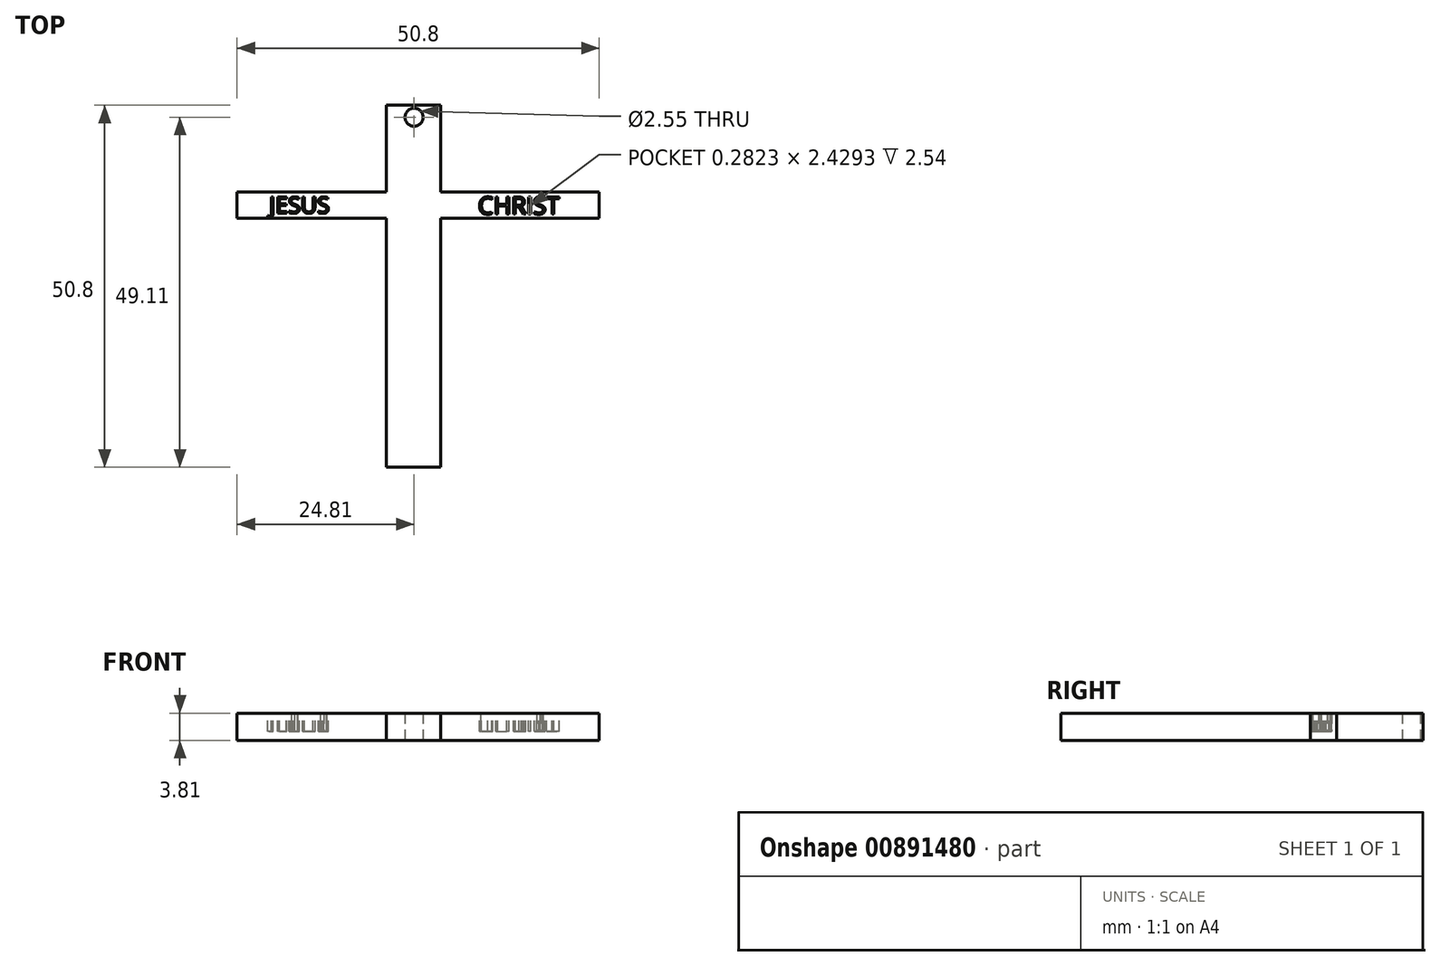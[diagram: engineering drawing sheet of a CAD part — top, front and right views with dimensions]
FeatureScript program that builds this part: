
annotation { "Feature Type Name" : "Feature", "Feature Type Description" : "" }
export const myFeature = defineFeature(function(context is Context, id is Id, definition is map)
    precondition{}
    {
        {
            var Q0;
            Q0=qCreatedBy(makeId("Top.planeOp"),FACE);
            var sketch = newSketch(context, id + "F0", { "sketchPlane" : qUnion([Q0])});
            skLineSegment(sketch, "E0.bottom", {"start": v(-3.9, 12.17) * mm, "end": v(3.73, 12.17) * mm});
            skLineSegment(sketch, "E0.top", {"start": v(-3.9, -38.63) * mm, "end": v(3.73, -38.63) * mm});
            skLineSegment(sketch, "E0.left", {"start": v(-3.9, 12.17) * mm, "end": v(-3.9, -38.63) * mm});
            skLineSegment(sketch, "E0.right", {"start": v(3.73, 12.17) * mm, "end": v(3.73, -38.63) * mm});
            skSolve(sketch);
        }
        {
            var Q0;
            Q0 = qSketchRegion(id + "F0", true);
            extrude(context, id + "F1", {"entities" : qUnion([Q0]), "depth" : 3.8 * mm, "offsetDistance" : 25.4 * mm});
        }
        {
            var Q0;
            Q0=qCreatedBy(makeId("Top.planeOp"),FACE);
            var sketch = newSketch(context, id + "F2", { "sketchPlane" : qUnion([Q0])});
            skLineSegment(sketch, "E1.bottom", {"start": v(-24.8, 0) * mm, "end": v(26, 0) * mm});
            skLineSegment(sketch, "E1.top", {"start": v(-24.8, -3.68) * mm, "end": v(26, -3.68) * mm});
            skLineSegment(sketch, "E1.left", {"start": v(-24.8, 0) * mm, "end": v(-24.8, -3.68) * mm});
            skLineSegment(sketch, "E1.right", {"start": v(26, 0) * mm, "end": v(26, -3.68) * mm});
            skSolve(sketch);
        }
        {
            var Q0;
            Q0 = qSketchRegion(id + "F2", true);
            extrude(context, id + "F3", {"entities" : qUnion([Q0]), "operationType" : NewBodyOperationType.ADD, "depth" : 3.8 * mm, "offsetDistance" : 25.4 * mm});
        }
        {
            var Q0;
            Q0=qCreatedBy(makeId("Top.planeOp"),FACE);
            var sketch = newSketch(context, id + "F4", { "sketchPlane" : qUnion([Q0])});
            skCircle(sketch, "E2", {"center": v(0, 10.48) * mm, "radius": 1.27 * mm});
            skSolve(sketch);
        }
        {
            var Q0;
            Q0 = qSketchRegion(id + "F4", true);
            extrude(context, id + "F5", {"entities" : qUnion([Q0]), "operationType" : NewBodyOperationType.REMOVE, "endBound" : BoundingType.THROUGH_ALL, "depth" : 25.4 * mm, "offsetDistance" : 25.4 * mm});
        }
        {
            var Q0;
            Q0=makeQuery(id+"F3.boolean.opBoolean","MERGE",FACE,{"derivedFrom":[makeQuery(id+"F1.opExtrude","CAP_FACE",FACE,{"disambiguationData":[OSD([sQuery(id+"F0.wireOp",EDGE,"E0.bottom"),sQuery(id+"F0.wireOp",EDGE,"E0.top"),sQuery(id+"F0.wireOp",EDGE,"E0.left"),sQuery(id+"F0.wireOp",EDGE,"E0.right")])],"isStart":false}),makeQuery(id+"F3.opExtrude","CAP_FACE",FACE,{"disambiguationData":[OSD([sQuery(id+"F2.wireOp",EDGE,"E1.bottom"),sQuery(id+"F2.wireOp",EDGE,"E1.top"),sQuery(id+"F2.wireOp",EDGE,"E1.left"),sQuery(id+"F2.wireOp",EDGE,"E1.right")])],"isStart":false})]});
            var sketch = newSketch(context, id + "F6", { "sketchPlane" : qUnion([Q0])});
            skText(sketch, "E3", { "text": "JESUS", "fontName": "OpenSans-Regular.ttf"});
            const initialGuessF6  = {"E3": [-0.0203, -0.00299, 1, 0, 0.0023]};
            skSetInitialGuess(sketch, initialGuessF6);
            skSolve(sketch);
        }
        {
            var Q0;
            Q0 = qSketchRegion(id + "F6", true);
            extrude(context, id + "F7", {"entities" : qUnion([Q0]), "operationType" : NewBodyOperationType.REMOVE, "oppositeDirection" : true, "depth" : 2.54 * mm, "offsetDistance" : 25.4 * mm});
        }
        {
            var Q0;
            Q0=makeQuery(id+"F3.boolean.opBoolean","MERGE",FACE,{"derivedFrom":[makeQuery(id+"F1.opExtrude","CAP_FACE",FACE,{"disambiguationData":[OSD([sQuery(id+"F0.wireOp",EDGE,"E0.bottom"),sQuery(id+"F0.wireOp",EDGE,"E0.top"),sQuery(id+"F0.wireOp",EDGE,"E0.left"),sQuery(id+"F0.wireOp",EDGE,"E0.right")])],"isStart":false}),makeQuery(id+"F3.opExtrude","CAP_FACE",FACE,{"disambiguationData":[OSD([sQuery(id+"F2.wireOp",EDGE,"E1.bottom"),sQuery(id+"F2.wireOp",EDGE,"E1.top"),sQuery(id+"F2.wireOp",EDGE,"E1.left"),sQuery(id+"F2.wireOp",EDGE,"E1.right")])],"isStart":false})]});
            var sketch = newSketch(context, id + "F8", { "sketchPlane" : qUnion([Q0])});
            skText(sketch, "E4", { "text": "CHRIST", "fontName": "OpenSans-Regular.ttf"});
            const initialGuessF8  = {"E4": [0.00897, -0.00313, 1, 0, 0.00245]};
            skSetInitialGuess(sketch, initialGuessF8);
            skSolve(sketch);
        }
        {
            var Q0;
            Q0 = qSketchRegion(id + "F8", true);
            extrude(context, id + "F9", {"entities" : qUnion([Q0]), "operationType" : NewBodyOperationType.REMOVE, "oppositeDirection" : true, "depth" : 2.54 * mm, "offsetDistance" : 25.4 * mm});
        }
    });
